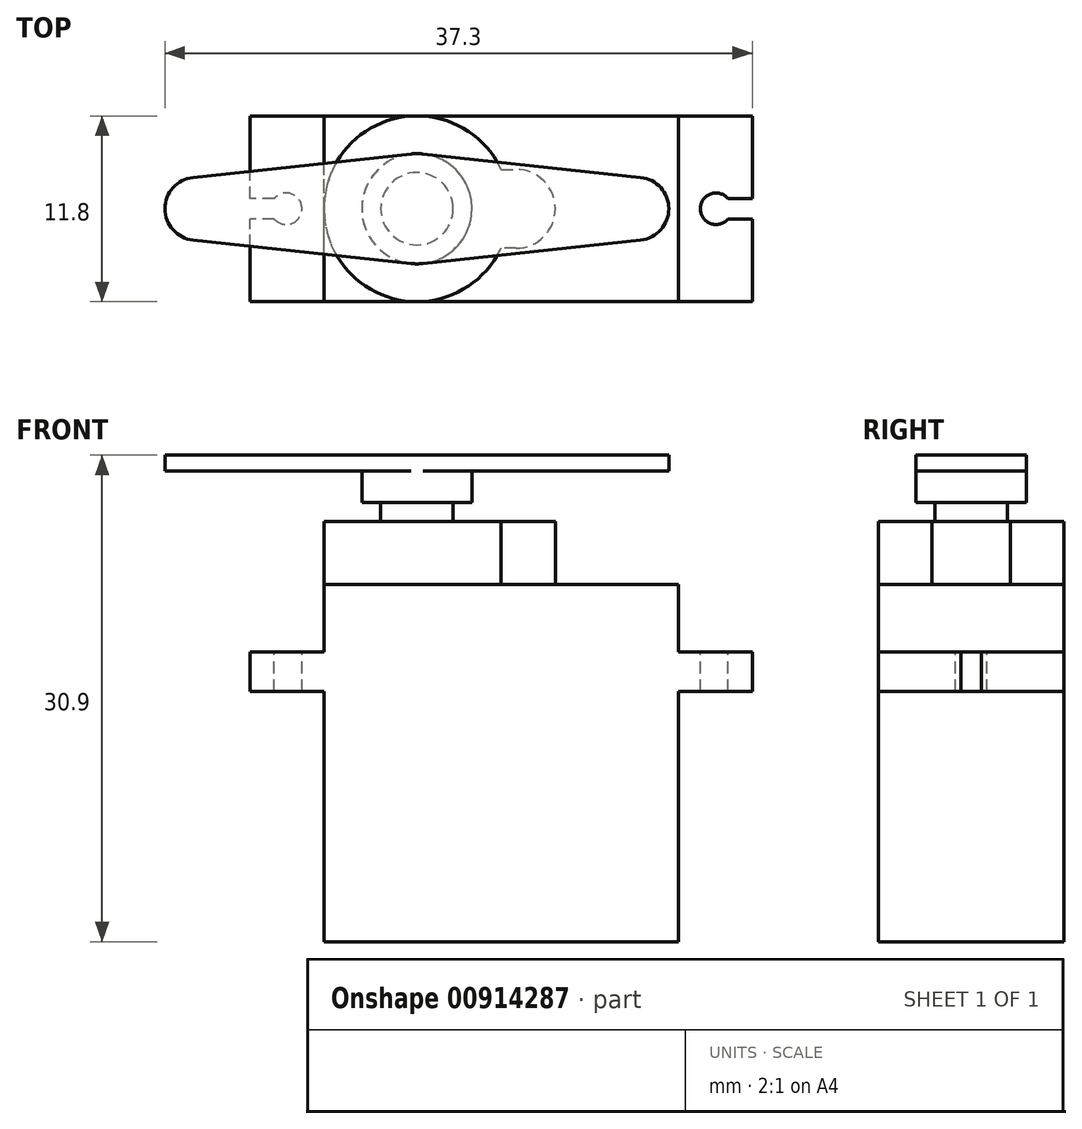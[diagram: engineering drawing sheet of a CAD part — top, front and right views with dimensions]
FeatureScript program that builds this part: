
annotation { "Feature Type Name" : "Feature", "Feature Type Description" : "" }
export const myFeature = defineFeature(function(context is Context, id is Id, definition is map)
    precondition{}
    {
        {
            var Q0;
            Q0=qCreatedBy(makeId("Front.planeOp"),FACE);
            var sketch = newSketch(context, id + "F0", { "sketchPlane" : qUnion([Q0])});
            skLineSegment(sketch, "E0.bottom", {"start": v(0, 0) * mm, "end": v(22.5, 0) * mm});
            skLineSegment(sketch, "E0.top", {"start": v(0, 22.7) * mm, "end": v(22.5, 22.7) * mm});
            skLineSegment(sketch, "E0.left", {"start": v(0, 0) * mm, "end": v(0, 22.7) * mm});
            skLineSegment(sketch, "E0.right", {"start": v(22.5, 0) * mm, "end": v(22.5, 22.7) * mm});
            skLineSegment(sketch, "E1.bottom", {"start": v(-4.7, 18.4) * mm, "end": v(27.2, 18.4) * mm});
            skLineSegment(sketch, "E1.top", {"start": v(-4.7, 15.9) * mm, "end": v(27.2, 15.9) * mm});
            skLineSegment(sketch, "E1.left", {"start": v(-4.7, 18.4) * mm, "end": v(-4.7, 15.9) * mm});
            skLineSegment(sketch, "E1.right", {"start": v(27.2, 18.4) * mm, "end": v(27.2, 15.9) * mm});
            skSolve(sketch);
        }
        {
            var Q0;
            Q0=qSketchRegion(id+"F0",true);
            extrude(context, id + "F1", {"entities" : qUnion([Q0]), "depth" : 11.8 * mm, "offsetDistance" : 25 * mm});
        }
        {
            var Q0;
            Q0=makeQuery(id+"F1.opExtrude","SWEPT_FACE",FACE,{"disambiguationData":[OSD([sQuery(id+"F0.wireOp",EDGE,"E0.top")])]});
            var sketch = newSketch(context, id + "F2", { "sketchPlane" : qUnion([Q0])});
            skCircle(sketch, "E2", {"center": v(5.9, -5.9) * mm, "radius": 5.9 * mm});
            skPoint(sketch, "E2.centerSnap0", {"position": v(0, -5.9) * mm});
            skCircle(sketch, "E3", {"center": v(12.2, -5.9) * mm, "radius": 2.5 * mm});
            skLineSegment(sketch, "E4", {"start": v(12.2, -8.4) * mm, "end": v(11.24, -8.4) * mm});
            skLineSegment(sketch, "E5", {"start": v(11.24, -3.4) * mm, "end": v(12.2, -3.4) * mm});
            skSolve(sketch);
        }
        {
            var Q0;
            Q0=qSketchRegion(id+"F2",true);
            var Q1;
            {var subQ0=sQuery(id+"F2.wireOp",EDGE,"E3");var subQ1=sQuery(id+"F2.wireOp",EDGE,"E2");var subQ2=makeQuery(id+"F2.imprint","INTERSECT",VERTEX,{"disambiguationData":[OD(0.0)],"derivedFrom":[subQ1,subQ0]});Q1=makeQuery(id+"F2.imprint","IMPRINT",FACE,{"disambiguationData":[TD([[makeQuery(id+"F2.imprint","IMPRINT",EDGE,{"disambiguationData":[TD([[subQ2,1.0]])],"derivedFrom":subQ1}),1.0]])]});}
            extrude(context, id + "F3", {"entities" : qUnion([Q0, Q1]), "operationType" : NewBodyOperationType.ADD, "depth" : 4 * mm, "offsetDistance" : 25 * mm});
        }
        {
            var Q0;
            {var subQ0=sQuery(id+"F0.wireOp",EDGE,"E1.bottom");Q0=makeQuery(id+"F1.opExtrude","SWEPT_FACE",FACE,{"disambiguationData":[OSD([subQ0]),TDD([makeQuery(id+"F0.imprint","IMPRINT",EDGE,{"disambiguationData":[TD([[makeQuery(id+"F0.imprint","INTERSECT",VERTEX,{"derivedFrom":[subQ0,sQuery(id+"F0.wireOp",EDGE,"E1.left")]}),-1.0]])],"derivedFrom":subQ0})])]});}
            var sketch = newSketch(context, id + "F4", { "sketchPlane" : qUnion([Q0])});
            skCircle(sketch, "E6", {"center": v(-2.4, -5.9) * mm, "radius": 1 * mm});
            skPoint(sketch, "E6.centerSnap0", {"position": v(-4.7, -5.9) * mm});
            skCircle(sketch, "E7", {"center": v(24.9, -5.9) * mm, "radius": 1 * mm});
            skLineSegment(sketch, "E8.bottom", {"start": v(-2.4, -5.25) * mm, "end": v(-7, -5.25) * mm});
            skLineSegment(sketch, "E8.top", {"start": v(-2.4, -6.55) * mm, "end": v(-7, -6.55) * mm});
            skLineSegment(sketch, "E8.left", {"start": v(-2.4, -5.25) * mm, "end": v(-2.4, -6.55) * mm});
            skLineSegment(sketch, "E8.right", {"start": v(-7, -5.25) * mm, "end": v(-7, -6.55) * mm});
            skLineSegment(sketch, "E9.bottom", {"start": v(24.9, -5.25) * mm, "end": v(29.55, -5.25) * mm});
            skLineSegment(sketch, "E9.top", {"start": v(24.9, -6.55) * mm, "end": v(29.55, -6.55) * mm});
            skLineSegment(sketch, "E9.left", {"start": v(24.9, -5.25) * mm, "end": v(24.9, -6.55) * mm});
            skLineSegment(sketch, "E9.right", {"start": v(29.55, -5.25) * mm, "end": v(29.55, -6.55) * mm});
            skPoint(sketch, "E9.middle", {"position": v(27.22, -5.9) * mm});
            skSolve(sketch);
        }
        {
            var Q0;
            Q0=qSketchRegion(id+"F4",true);
            extrude(context, id + "F5", {"entities" : qUnion([Q0]), "operationType" : NewBodyOperationType.REMOVE, "endBound" : BoundingType.THROUGH_ALL, "oppositeDirection" : true, "depth" : 25 * mm, "offsetDistance" : 25 * mm});
        }
        {
            var Q0;
            Q0=makeQuery(id+"F3.opExtrude","CAP_FACE",FACE,{"disambiguationData":[OSD([sQuery(id+"F2.wireOp",EDGE,"E2"),sQuery(id+"F2.wireOp",EDGE,"E3"),sQuery(id+"F2.wireOp",EDGE,"E4"),sQuery(id+"F2.wireOp",EDGE,"E5")])],"isStart":false});
            var sketch = newSketch(context, id + "F6", { "sketchPlane" : qUnion([Q0])});
            skCircle(sketch, "E10", {"center": v(5.9, -5.9) * mm, "radius": 2.3 * mm});
            skSolve(sketch);
        }
        {
            var Q0;
            Q0=qSketchRegion(id+"F6",true);
            extrude(context, id + "F7", {"entities" : qUnion([Q0]), "depth" : 3.2 * mm, "offsetDistance" : 25 * mm});
        }
        {
            var Q0;
            Q0=makeQuery(id+"F7.opExtrude","CAP_FACE",FACE,{"disambiguationData":[OSD([sQuery(id+"F6.wireOp",EDGE,"E10")])],"isStart":false});
            var sketch = newSketch(context, id + "F8", { "sketchPlane" : qUnion([Q0])});
            skCircle(sketch, "E11", {"center": v(5.9, -5.9) * mm, "radius": 3.5 * mm});
            skCircle(sketch, "E12", {"center": v(-8.1, -5.9) * mm, "radius": 2 * mm});
            skLineSegment(sketch, "E13", {"start": v(-8.31, -3.91) * mm, "end": v(5.53, -2.42) * mm});
            skLineSegment(sketch, "E14", {"start": v(5.9, -5.9) * mm, "end": v(5.9, -2.4) * mm, "construction": true});
            skLineSegment(sketch, "E15", {"start": v(5.9, -5.9) * mm, "end": v(2.4, -5.9) * mm, "construction": true});
            skLineSegment(sketch, "E16.MirrorCS", {"start": v(20.11, -3.91) * mm, "end": v(6.27, -2.42) * mm});
            skCircle(sketch, "E17.MirrorC", {"center": v(19.9, -5.9) * mm, "radius": 2 * mm});
            skLineSegment(sketch, "E18.MirrorCS", {"start": v(-8.31, -7.89) * mm, "end": v(5.53, -9.38) * mm});
            skLineSegment(sketch, "E19.MirrorCS", {"start": v(20.11, -7.89) * mm, "end": v(6.27, -9.38) * mm});
            skSolve(sketch);
        }
        {
            var Q0;
            Q0=qSketchRegion(id+"F8",true);
            extrude(context, id + "F9", {"entities" : qUnion([Q0]), "operationType" : NewBodyOperationType.ADD, "depth" : 1 * mm, "offsetDistance" : 25 * mm});
        }
        {
            var Q0;
            Q0=makeQuery(id+"F8.imprint","IMPRINT",FACE,{"disambiguationData":[TD([[makeQuery(id+"F8.imprint","IMPRINT",EDGE,{"derivedFrom":makeQuery(id+"F7.opExtrude","CAP_EDGE",EDGE,{"disambiguationData":[OSD([sQuery(id+"F6.wireOp",EDGE,"E10")])],"isStart":false})}),-1.0]])]});
            extrude(context, id + "F10", {"entities" : qUnion([Q0]), "operationType" : NewBodyOperationType.ADD, "oppositeDirection" : true, "depth" : 2 * mm, "offsetDistance" : 25 * mm});
        }
    });
